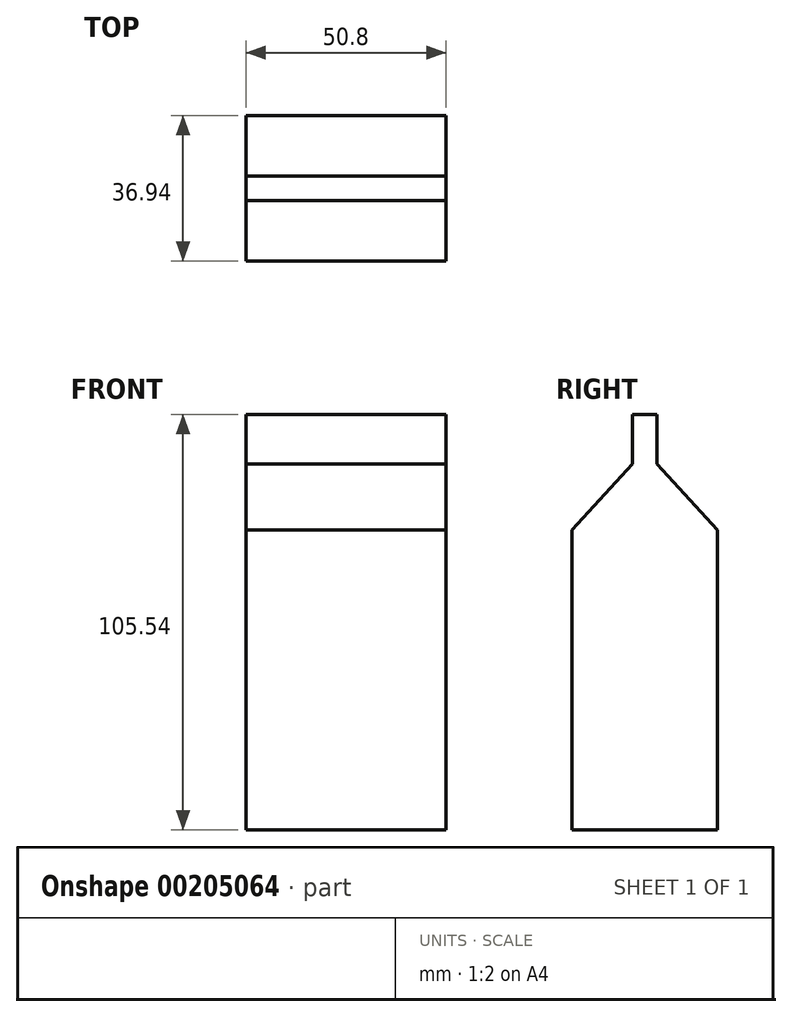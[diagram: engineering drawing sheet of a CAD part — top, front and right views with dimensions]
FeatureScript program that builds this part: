
annotation { "Feature Type Name" : "Feature", "Feature Type Description" : "" }
export const myFeature = defineFeature(function(context is Context, id is Id, definition is map)
    precondition{}
    {
        {
            var Q0;
            Q0=qCreatedBy(makeId("Right.planeOp"),FACE);
            var sketch = newSketch(context, id + "F0", { "sketchPlane" : qUnion([Q0])});
            skLineSegment(sketch, "E0.bottom", {"start": v(18.47, -38.08) * mm, "end": v(-18.47, -38.08) * mm});
            skLineSegment(sketch, "E0.left", {"start": v(18.47, -38.08) * mm, "end": v(18.47, 38.08) * mm});
            skLineSegment(sketch, "E0.right", {"start": v(-18.47, -38.08) * mm, "end": v(-18.47, 38.08) * mm});
            skPoint(sketch, "E0.middle", {"position": v(0, 0) * mm});
            skLineSegment(sketch, "E1", {"start": v(3.13, 54.85) * mm, "end": v(18.47, 38.08) * mm});
            skLineSegment(sketch, "E2", {"start": v(3.13, 67.46) * mm, "end": v(3.13, 54.85) * mm});
            skLineSegment(sketch, "E3", {"start": v(3.13, 67.46) * mm, "end": v(0, 67.46) * mm});
            skLineSegment(sketch, "E4.MirrorCS", {"start": v(-3.13, 67.46) * mm, "end": v(-3.13, 54.85) * mm});
            skLineSegment(sketch, "E5.MirrorCS", {"start": v(-3.13, 54.85) * mm, "end": v(-18.47, 38.08) * mm});
            skLineSegment(sketch, "E6.MirrorCS", {"start": v(-3.13, 67.46) * mm, "end": v(0, 67.46) * mm});
            skSolve(sketch);
        }
        {
            var Q0;
            Q0 = qSketchRegion(id + "F0", true);
            extrude(context, id + "F1", {"entities" : qUnion([Q0]), "depth" : 25.4 * mm, "hasSecondDirection" : true, "secondDirectionOppositeDirection" : true, "secondDirectionDepth" : 25.4 * mm});
        }
    });
